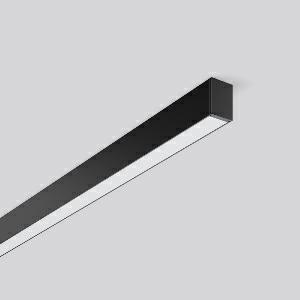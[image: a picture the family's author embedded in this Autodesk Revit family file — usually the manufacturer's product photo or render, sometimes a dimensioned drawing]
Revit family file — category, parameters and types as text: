
# Revit family: less_is_more_27_312200_003_1_76_0e52
name_source: partatom
category: Lighting Fixtures
units: mm (PartAtom-declared; Revit-internal decimal feet)

## family parameters
Cut with Voids When Loaded = No
Host = Face
Light Source = No
Part Type = Normal
Room Calculation Point = No
Round Connector Dimension = Use Diameter
Shared = No

## types (1)
- LESS IS MORE 27 (1 x LED Modul 840, 2400 lm, 4000)
    Apparent Load = 39 VA
    CIE Flux Codes = 48 79 96 100 100
    Color Rendering = 80
    Color Temperature = 4000
    Default Elevation = 1800 mm
    Description = Series: LESS IS MORE 27
Ceiling and wall luminaire with slim design. Housing: extruded aluminium profile, powder-coated. End cap aluminium powder-coated. Diffuser made of non-yellowing plastic (PMMA), opal. Suitable for Ceiling mounting, Wall (surface). External driver with connecting cable. 
Colour: deep black, matt (RAL 9005)
Length: 1512 mm
Width: 28 mm
Height: 38 mm
Lamp: LED
Socket: without socket
Colour temperature: 4000K
Colour rendering index (CRI): 82
System power: 39 W
Rated luminous flux: 2400 lm
Luminous efficiency: 62 lm/W
Control gear: Voltage converter, DALI dim.
Protection class: II
Type of protection: IP 20
    Height = 38 mm
    Lamp = 1 x LED Modul 840
    Lamp Light Flux = 2400 lm
    Lamp count = 1
    Length = 1512 mm
    Lifetime = 50000 h
    Luminous efficacy = 62 lm/W
    Manufacturer = RZB
    ModVariant = No
    Model = 312200.003.1.76
    Mounting Place = Ceiling, Wall
    Mounting Type = Surface mounted
    Number of Poles = 1
    OnlyDefault = Yes
    Power Factor = 1
    Product Name = LESS IS MORE 27
    Product group = Surface mounted LED linear luminaires
    ProductGroupID = 307
    Protection Class = Protection class II
    Protection Degree = IP 20
    RLX_Detail_Level = 1
    RLX_Emergency_Light_Flux = 0 lm
    RLX_Emergency_Type = 0
    RLX_Emergency_Type_DB = No
    RlxData = <blob elided: 28753 chars, md5=08d6b4d4>
    Socket = socket
    Standby Power = 0 W
    System Light Flux = 2400 lm
    System Power = 39 W
    Type Comments = Product without accessories
    Type Image = 312196.003.jpg
    URL = http://relux.com
    VarID = ---
    Voltage = 230 V
    Voltage Range = 220-240 V
    Weight = 0.00 kg
    Width = 28 mm

## geometry (parser evidence)
native form markers: Blend x4, Sweep x11
no freeform markers — native parametric forms only
